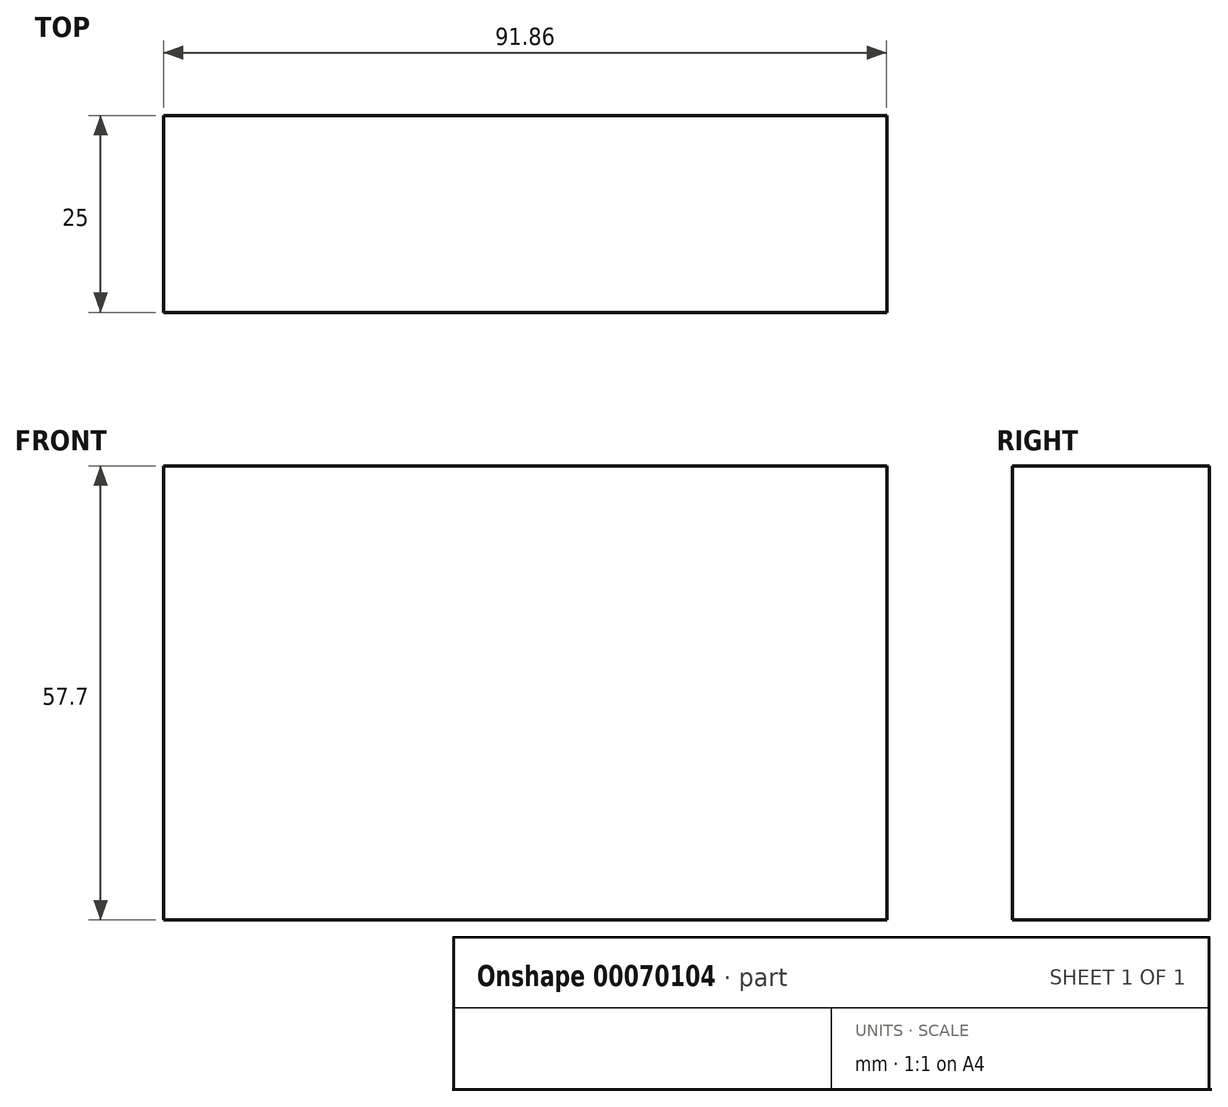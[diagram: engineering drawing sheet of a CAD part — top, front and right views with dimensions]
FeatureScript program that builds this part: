
annotation { "Feature Type Name" : "Feature", "Feature Type Description" : "" }
export const myFeature = defineFeature(function(context is Context, id is Id, definition is map)
    precondition{}
    {
        {
            var Q0;
            Q0=qCreatedBy(makeId("Front.planeOp"),FACE);
            var sketch = newSketch(context, id + "F0", { "sketchPlane" : qUnion([Q0])});
            skLineSegment(sketch, "E0.bottom", {"start": v(-42, 26.54) * mm, "end": v(49.85, 26.54) * mm});
            skLineSegment(sketch, "E0.top", {"start": v(-42, -31.16) * mm, "end": v(49.85, -31.16) * mm});
            skLineSegment(sketch, "E0.left", {"start": v(-42, 26.54) * mm, "end": v(-42, -31.16) * mm});
            skLineSegment(sketch, "E0.right", {"start": v(49.85, 26.54) * mm, "end": v(49.85, -31.16) * mm});
            skSolve(sketch);
        }
        {
            var Q0;
            Q0=makeQuery(id+"F0.imprint","IMPRINT",FACE,{"disambiguationData":[TD([[makeQuery(id+"F0.imprint","IMPRINT",EDGE,{"derivedFrom":sQuery(id+"F0.wireOp",EDGE,"E0.bottom")}),-1.0]])]});
            extrude(context, id + "F1", {"entities" : qUnion([Q0]), "depth" : 25 * mm});
        }
    });
